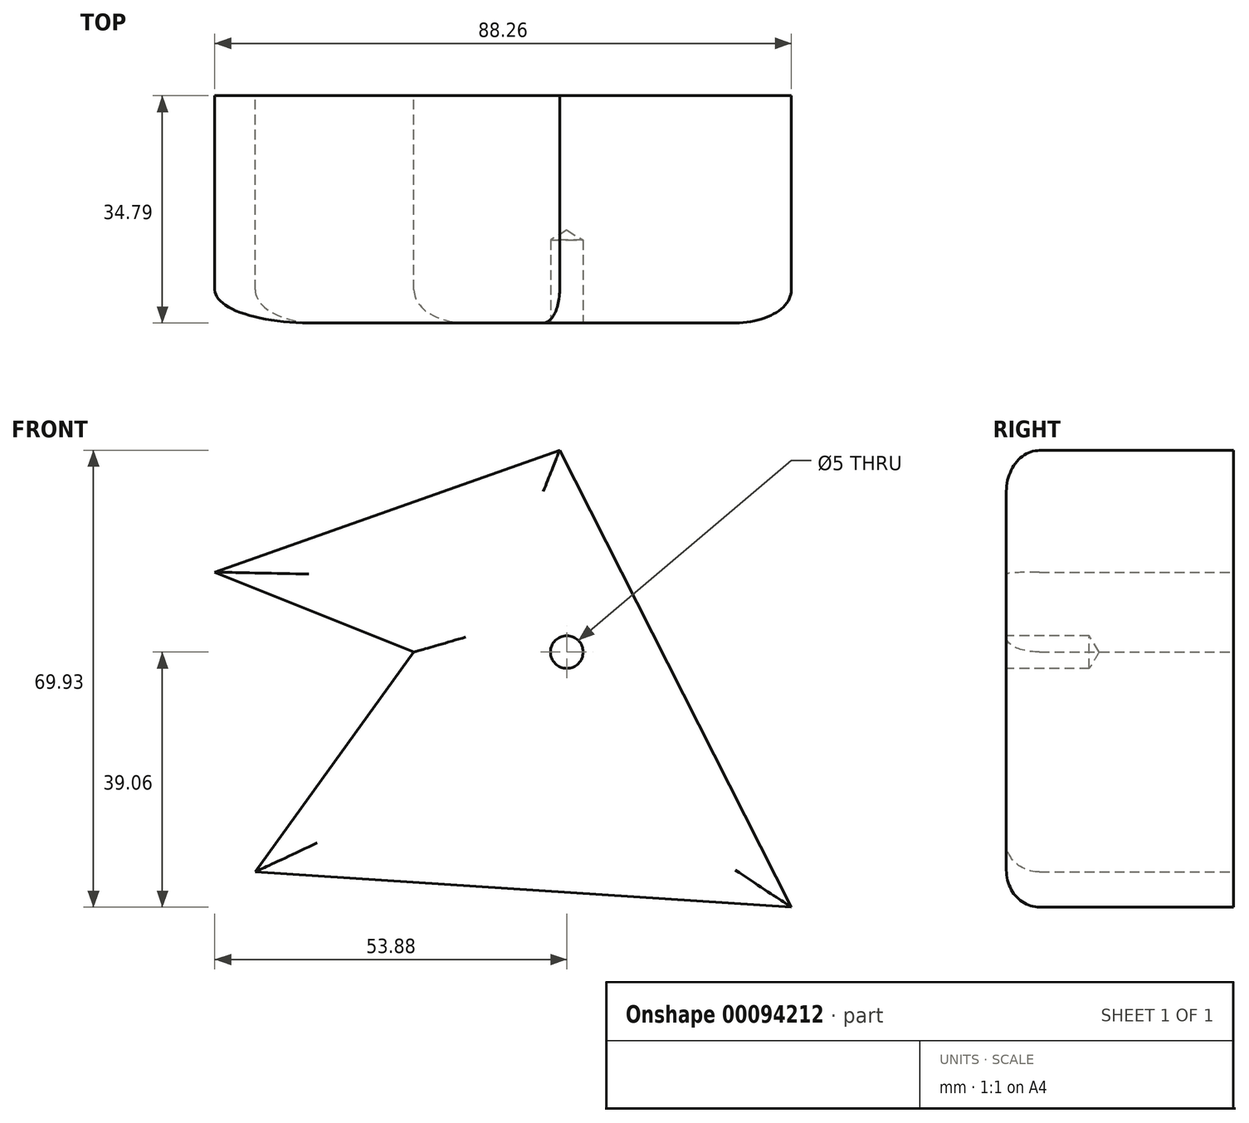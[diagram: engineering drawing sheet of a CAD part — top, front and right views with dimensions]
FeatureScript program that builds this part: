
annotation { "Feature Type Name" : "Feature", "Feature Type Description" : "" }
export const myFeature = defineFeature(function(context is Context, id is Id, definition is map)
    precondition{}
    {
        {
            var Q0;
            Q0=qCreatedBy(makeId("Front.planeOp"),FACE);
            var sketch = newSketch(context, id + "F0", { "sketchPlane" : qUnion([Q0])});
            skLineSegment(sketch, "E0", {"start": v(-43.9, 32.13) * mm, "end": v(8.9, 50.76) * mm});
            skLineSegment(sketch, "E1", {"start": v(8.9, 50.76) * mm, "end": v(44.37, -19.17) * mm});
            skLineSegment(sketch, "E2", {"start": v(44.37, -19.17) * mm, "end": v(-37.7, -13.77) * mm});
            skLineSegment(sketch, "E3", {"start": v(-37.7, -13.77) * mm, "end": v(-13.41, 19.9) * mm});
            skLineSegment(sketch, "E4", {"start": v(-13.41, 19.9) * mm, "end": v(-43.9, 32.13) * mm});
            skSolve(sketch);
        }
        {
            var Q0;
            Q0=makeQuery(id+"F0.imprint","IMPRINT",FACE,{"disambiguationData":[TD([[makeQuery(id+"F0.imprint","IMPRINT",EDGE,{"derivedFrom":sQuery(id+"F0.wireOp",EDGE,"E0")}),-1.0]])]});
            extrude(context, id + "F1", {"entities" : qUnion([Q0]), "depth" : 34.8 * mm});
        }
        {
            var Q0;
            Q0=makeQuery(id+"F1.opExtrude","CAP_EDGE",EDGE,{"disambiguationData":[OSD([sQuery(id+"F0.wireOp",EDGE,"E0")])],"isStart":false});
            var Q1;
            Q1=makeQuery(id+"F1.opExtrude","CAP_EDGE",EDGE,{"disambiguationData":[OSD([sQuery(id+"F0.wireOp",EDGE,"E1")])],"isStart":false});
            var Q2;
            Q2=makeQuery(id+"F1.opExtrude","CAP_EDGE",EDGE,{"disambiguationData":[OSD([sQuery(id+"F0.wireOp",EDGE,"E2")])],"isStart":false});
            var Q3;
            Q3=makeQuery(id+"F1.opExtrude","CAP_EDGE",EDGE,{"disambiguationData":[OSD([sQuery(id+"F0.wireOp",EDGE,"E3")])],"isStart":false});
            var Q4;
            Q4=makeQuery(id+"F1.opExtrude","CAP_EDGE",EDGE,{"disambiguationData":[OSD([sQuery(id+"F0.wireOp",EDGE,"E4")])],"isStart":false});
            fillet(context, id + "F2", {"entities" : qUnion([Q0, Q1, Q2, Q3, Q4]), "radius" : 5.08 * mm, "tangentPropagation" : true, "allowEdgeOverflow" : false});
        }
        {
            var Q0;
            Q0=makeQuery(id+"F1.opExtrude","CAP_FACE",FACE,{"disambiguationData":[OSD([sQuery(id+"F0.wireOp",EDGE,"E0"),sQuery(id+"F0.wireOp",EDGE,"E1"),sQuery(id+"F0.wireOp",EDGE,"E2"),sQuery(id+"F0.wireOp",EDGE,"E3"),sQuery(id+"F0.wireOp",EDGE,"E4")])],"isStart":false});
            var sketch = newSketch(context, id + "F3", { "sketchPlane" : qUnion([Q0])});
            skPoint(sketch, "E5", {"position": v(9.99, 19.9) * mm});
            skPoint(sketch, "E6", {"position": v(4.59, 8.2) * mm});
            skPoint(sketch, "E7", {"position": v(17.55, -4.41) * mm});
            skSolve(sketch);
        }
        {
            var Q0;
            Q0=sQuery(id+"F3.wireOp",VERTEX,"E5");
            var Q1;
            Q1=makeQuery(id+"F1.opExtrude","SWEPT_BODY",BODY,{"disambiguationData":[OSD([sQuery(id+"F0.wireOp",EDGE,"E0"),sQuery(id+"F0.wireOp",EDGE,"E1"),sQuery(id+"F0.wireOp",EDGE,"E2"),sQuery(id+"F0.wireOp",EDGE,"E3"),sQuery(id+"F0.wireOp",EDGE,"E4")])]});
            hole(context, id + "F4", {"style" : HoleStyle.SIMPLE, "endStyle" : HoleEndStyle.BLIND, "standardTappedOrClearance" : lookupTablePath({ "standard" : "ISO", "size" : "5", "type" : "Drilled" }), "standardBlindInLast" : lookupTablePath({ "standard" : "ISO", "size" : "5", "type" : "Drilled" }), "holeDiameter" : 5 * mm, "holeDepth" : 12.7 * mm, "locations" : qUnion([Q0]), "scope" : qUnion([Q1])});
        }
    });
